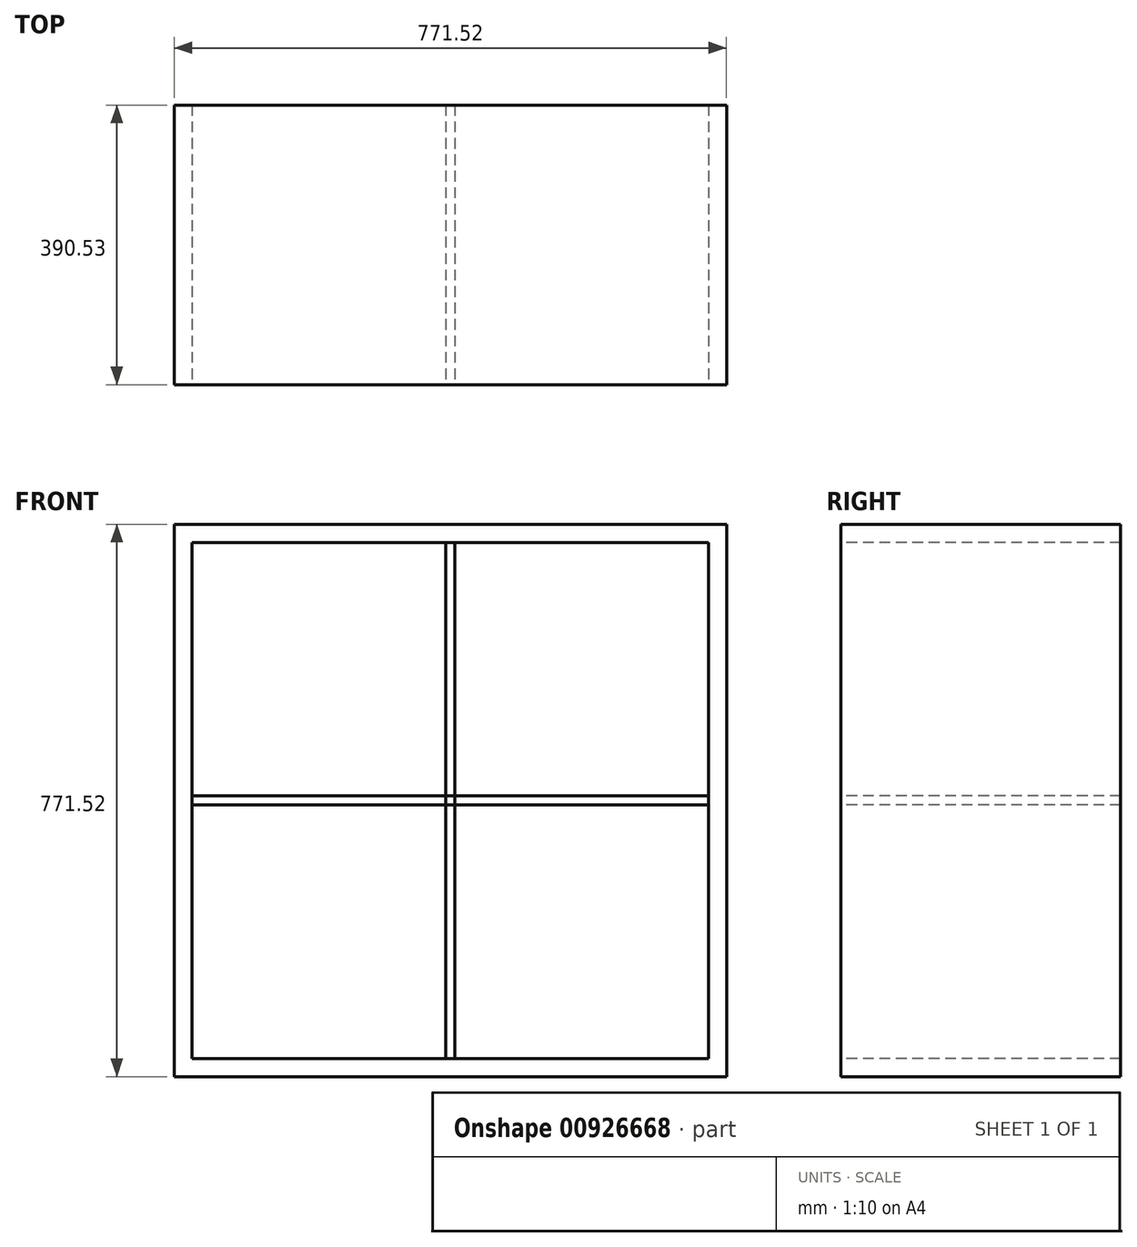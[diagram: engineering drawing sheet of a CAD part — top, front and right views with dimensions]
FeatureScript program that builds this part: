
annotation { "Feature Type Name" : "Feature", "Feature Type Description" : "" }
export const myFeature = defineFeature(function(context is Context, id is Id, definition is map)
    precondition{}
    {
        {
            var Q0;
            Q0=qCreatedBy(makeId("Front.planeOp"),FACE);
            var sketch = newSketch(context, id + "F0", { "sketchPlane" : qUnion([Q0])});
            skLineSegment(sketch, "E0.bottom", {"start": v(385.76, -385.76) * mm, "end": v(-385.76, -385.76) * mm});
            skLineSegment(sketch, "E0.top", {"start": v(385.76, 385.76) * mm, "end": v(-385.76, 385.76) * mm});
            skLineSegment(sketch, "E0.left", {"start": v(385.76, -385.76) * mm, "end": v(385.76, 385.76) * mm});
            skLineSegment(sketch, "E0.right", {"start": v(-385.76, -385.76) * mm, "end": v(-385.76, 385.76) * mm});
            skLineSegment(sketch, "E1.bottom", {"start": v(360.36, -360.36) * mm, "end": v(-360.36, -360.36) * mm});
            skLineSegment(sketch, "E1.top", {"start": v(360.36, 360.36) * mm, "end": v(-360.36, 360.36) * mm});
            skLineSegment(sketch, "E1.left", {"start": v(360.36, -360.36) * mm, "end": v(360.36, 360.36) * mm});
            skLineSegment(sketch, "E1.right", {"start": v(-360.36, -360.36) * mm, "end": v(-360.36, 360.36) * mm});
            skLineSegment(sketch, "E2.bottom", {"start": v(6.35, 360.36) * mm, "end": v(-6.35, 360.36) * mm});
            skLineSegment(sketch, "E2.top", {"start": v(6.35, -360.36) * mm, "end": v(-6.35, -360.36) * mm});
            skLineSegment(sketch, "E3.left", {"start": v(360.36, -6.35) * mm, "end": v(360.36, 6.35) * mm});
            skLineSegment(sketch, "E3.right", {"start": v(-360.36, -6.35) * mm, "end": v(-360.36, 6.35) * mm});
            skSolve(sketch);
        }
        {
            var Q0;
            Q0=makeQuery(id+"F0.imprint","IMPRINT",FACE,{"disambiguationData":[TD([[makeQuery(id+"F0.imprint","IMPRINT",EDGE,{"derivedFrom":sQuery(id+"F0.wireOp",EDGE,"E0.bottom")}),-1.0]])]});
            extrude(context, id + "F1", {"entities" : qUnion([Q0]), "depth" : 390.52 * mm, "offsetDistance" : 25.4 * mm});
        }
        {
            var Q0;
            Q0=makeQuery(id+"F1.opExtrude","CAP_FACE",FACE,{"disambiguationData":[OSD([sQuery(id+"F0.wireOp",EDGE,"E0.bottom"),sQuery(id+"F0.wireOp",EDGE,"E0.top"),sQuery(id+"F0.wireOp",EDGE,"E0.left"),sQuery(id+"F0.wireOp",EDGE,"E0.right"),sQuery(id+"F0.wireOp",EDGE,"E1.bottom"),sQuery(id+"F0.wireOp",EDGE,"E1.top"),sQuery(id+"F0.wireOp",EDGE,"E1.left"),sQuery(id+"F0.wireOp",EDGE,"E1.right")])],"isStart":false});
            var sketch = newSketch(context, id + "F2", { "sketchPlane" : qUnion([Q0])});
            skLineSegment(sketch, "E4.bottom", {"start": v(360.36, -6.35) * mm, "end": v(-360.36, -6.35) * mm});
            skLineSegment(sketch, "E4.top", {"start": v(360.36, 6.35) * mm, "end": v(-360.36, 6.35) * mm});
            skLineSegment(sketch, "E4.left", {"start": v(360.36, -6.35) * mm, "end": v(360.36, 6.35) * mm});
            skLineSegment(sketch, "E4.right", {"start": v(-360.36, -6.35) * mm, "end": v(-360.36, 6.35) * mm});
            skPoint(sketch, "E4.middle", {"position": v(0, 0) * mm});
            skSolve(sketch);
        }
        {
            var Q0;
            Q0 = qSketchRegion(id + "F2", true);
            extrude(context, id + "F3", {"entities" : qUnion([Q0]), "depth" : -390.52 * mm, "offsetDistance" : 25.4 * mm});
        }
        {
            var Q0;
            Q0=makeQuery(id+"F1.opExtrude","CAP_FACE",FACE,{"disambiguationData":[OSD([sQuery(id+"F0.wireOp",EDGE,"E0.bottom"),sQuery(id+"F0.wireOp",EDGE,"E0.top"),sQuery(id+"F0.wireOp",EDGE,"E0.left"),sQuery(id+"F0.wireOp",EDGE,"E0.right"),sQuery(id+"F0.wireOp",EDGE,"E1.bottom"),sQuery(id+"F0.wireOp",EDGE,"E1.top"),sQuery(id+"F0.wireOp",EDGE,"E1.left"),sQuery(id+"F0.wireOp",EDGE,"E1.right")])],"isStart":false});
            var sketch = newSketch(context, id + "F4", { "sketchPlane" : qUnion([Q0])});
            skLineSegment(sketch, "E5.bottom", {"start": v(6.35, 360.36) * mm, "end": v(-6.35, 360.36) * mm});
            skLineSegment(sketch, "E5.top", {"start": v(6.35, -360.36) * mm, "end": v(-6.35, -360.36) * mm});
            skLineSegment(sketch, "E5.left", {"start": v(6.35, 360.36) * mm, "end": v(6.35, -360.36) * mm});
            skLineSegment(sketch, "E5.right", {"start": v(-6.35, 360.36) * mm, "end": v(-6.35, -360.36) * mm});
            skPoint(sketch, "E5.middle", {"position": v(0, 0) * mm});
            skSolve(sketch);
        }
        {
            var Q0;
            Q0 = qSketchRegion(id + "F4", true);
            extrude(context, id + "F5", {"entities" : qUnion([Q0]), "depth" : -390.52 * mm, "offsetDistance" : 25.4 * mm});
        }
    });
